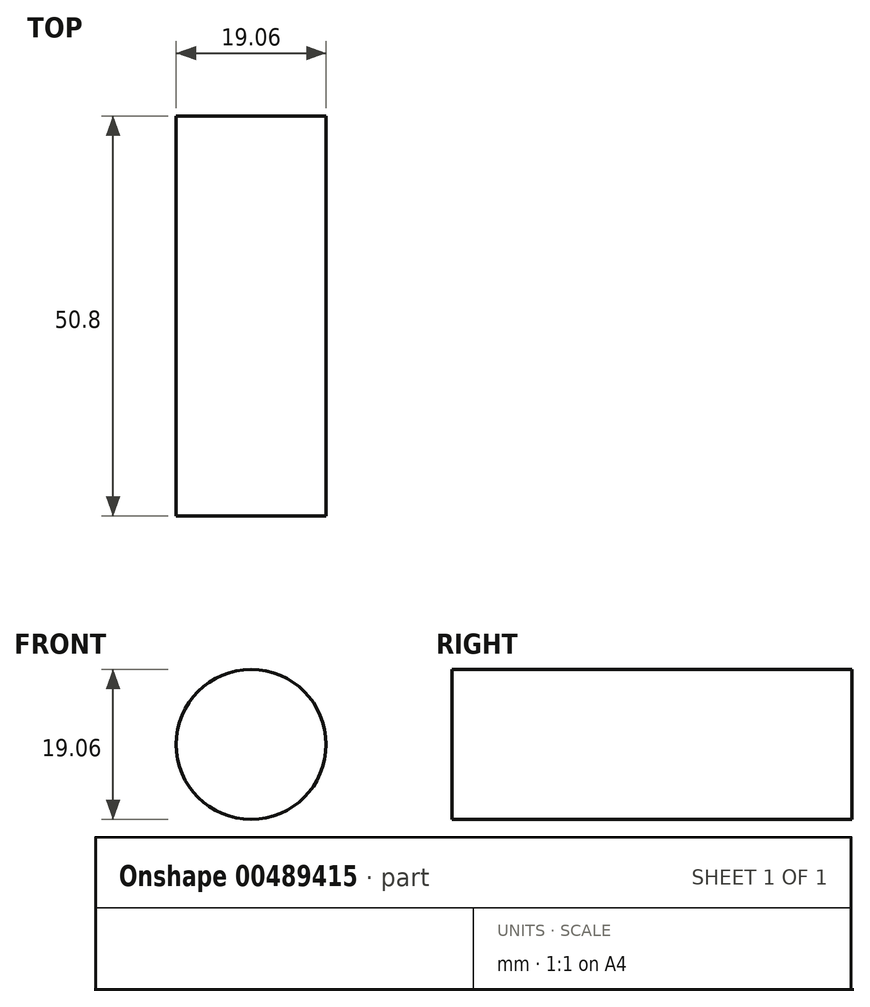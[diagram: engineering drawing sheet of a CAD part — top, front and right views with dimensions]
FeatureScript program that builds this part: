
annotation { "Feature Type Name" : "Feature", "Feature Type Description" : "" }
export const myFeature = defineFeature(function(context is Context, id is Id, definition is map)
    precondition{}
    {
        {
            var Q0;
            Q0=qCreatedBy(makeId("Front.planeOp"),FACE);
            var sketch = newSketch(context, id + "F0", { "sketchPlane" : qUnion([Q0])});
            skCircle(sketch, "E0", {"center": v(0, 0) * mm, "radius": 9.53 * mm});
            skSolve(sketch);
        }
        {
            var Q0;
            Q0 = qSketchRegion(id + "F0", true);
            extrude(context, id + "F1", {"entities" : qUnion([Q0]), "depth" : 50.8 * mm, "offsetDistance" : 25.4 * mm});
        }
    });
